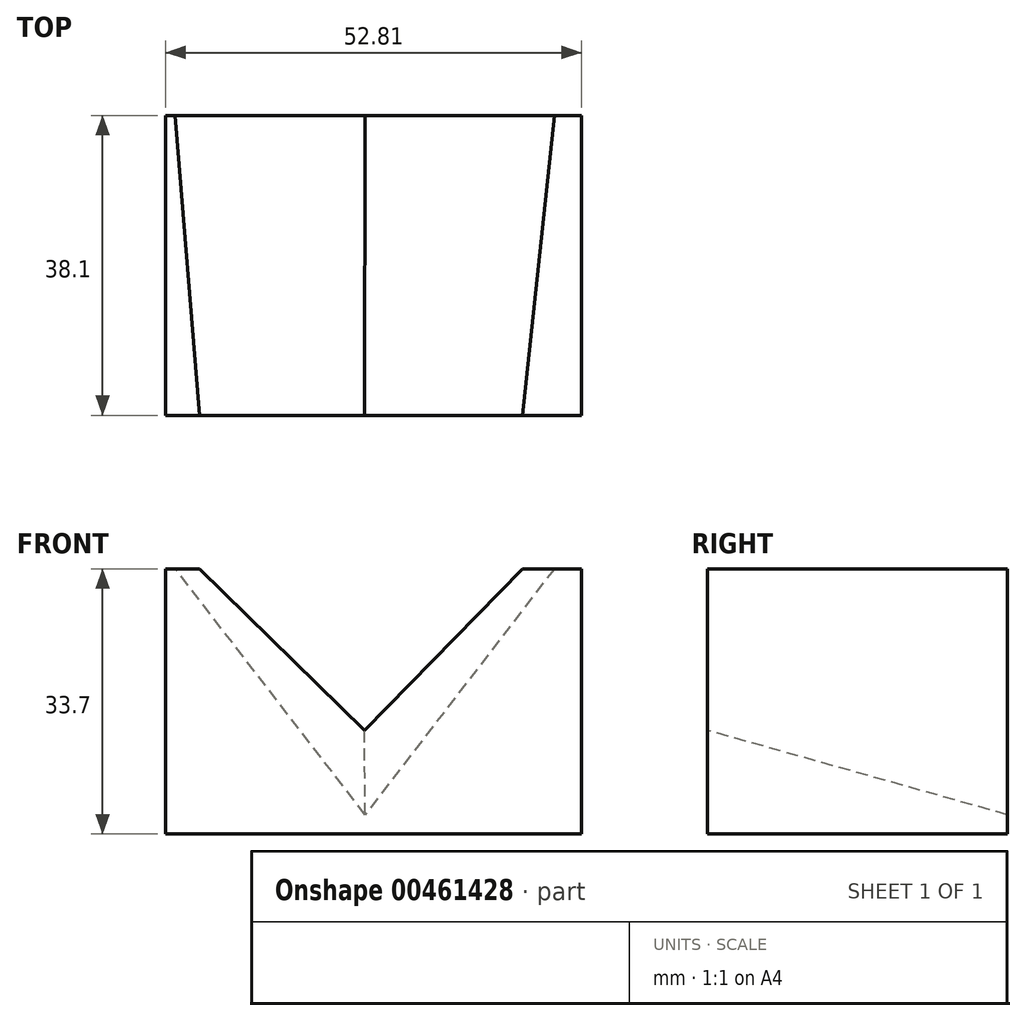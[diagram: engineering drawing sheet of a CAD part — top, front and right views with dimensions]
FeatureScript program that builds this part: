
annotation { "Feature Type Name" : "Feature", "Feature Type Description" : "" }
export const myFeature = defineFeature(function(context is Context, id is Id, definition is map)
    precondition{}
    {
        {
            var Q0;
            Q0=qCreatedBy(makeId("Front.planeOp"),FACE);
            var sketch = newSketch(context, id + "F0", { "sketchPlane" : qUnion([Q0])});
            skLineSegment(sketch, "E0.bottom", {"start": v(-31.33, 22.07) * mm, "end": v(21.48, 22.07) * mm});
            skLineSegment(sketch, "E0.top", {"start": v(-31.33, -11.63) * mm, "end": v(21.48, -11.63) * mm});
            skLineSegment(sketch, "E0.left", {"start": v(-31.33, 22.07) * mm, "end": v(-31.33, -11.63) * mm});
            skLineSegment(sketch, "E0.right", {"start": v(21.48, 22.07) * mm, "end": v(21.48, -11.63) * mm});
            skSolve(sketch);
        }
        {
            var Q0;
            Q0=makeQuery(id+"F0.imprint","IMPRINT",FACE,{"disambiguationData":[TD([[makeQuery(id+"F0.imprint","IMPRINT",EDGE,{"derivedFrom":sQuery(id+"F0.wireOp",EDGE,"E0.bottom")}),-1.0]])]});
            extrude(context, id + "F1", {"entities" : qUnion([Q0]), "depth" : 38.1 * mm});
        }
        {
            var Q0;
            Q0=makeQuery(id+"F1.opExtrude","CAP_FACE",FACE,{"disambiguationData":[OSD([sQuery(id+"F0.wireOp",EDGE,"E0.bottom"),sQuery(id+"F0.wireOp",EDGE,"E0.top"),sQuery(id+"F0.wireOp",EDGE,"E0.left"),sQuery(id+"F0.wireOp",EDGE,"E0.right")])],"isStart":false});
            var sketch = newSketch(context, id + "F2", { "sketchPlane" : qUnion([Q0])});
            skLineSegment(sketch, "E1", {"start": v(-27.05, 22.07) * mm, "end": v(-6.07, 1.54) * mm});
            skLineSegment(sketch, "E2", {"start": v(-6.07, 1.54) * mm, "end": v(14.02, 22.07) * mm});
            skSolve(sketch);
        }
        {
            var Q0;
            Q0=makeQuery(id+"F1.opExtrude","CAP_FACE",FACE,{"disambiguationData":[OSD([sQuery(id+"F0.wireOp",EDGE,"E0.bottom"),sQuery(id+"F0.wireOp",EDGE,"E0.top"),sQuery(id+"F0.wireOp",EDGE,"E0.left"),sQuery(id+"F0.wireOp",EDGE,"E0.right")])],"isStart":true});
            var sketch = newSketch(context, id + "F3", { "sketchPlane" : qUnion([Q0])});
            skLineSegment(sketch, "E3", {"start": v(-18.03, 22.07) * mm, "end": v(6, -9.16) * mm});
            skLineSegment(sketch, "E4", {"start": v(6, -9.16) * mm, "end": v(30.1, 22.07) * mm});
            skSolve(sketch);
        }
        {
            var Q1;
            {var subQ0=sQuery(id+"F3.wireOp",EDGE,"E3");Q1=makeQuery(id+"F3.imprint","IMPRINT",FACE,{"disambiguationData":[TD([[makeQuery(id+"F3.imprint","IMPRINT",EDGE,{"derivedFrom":subQ0}),1.0]])]});}
            var Q2;
            {var subQ0=sQuery(id+"F2.wireOp",EDGE,"E1");Q2=makeQuery(id+"F2.imprint","IMPRINT",FACE,{"disambiguationData":[TD([[makeQuery(id+"F2.imprint","IMPRINT",EDGE,{"derivedFrom":subQ0}),1.0]])]});}
            var Q3;
            {var subQ0=sQuery(id+"F3.wireOp",EDGE,"E3");Q3=makeQuery(id+"F3.imprint","IMPRINT",FACE,{"disambiguationData":[TD([[makeQuery(id+"F3.imprint","IMPRINT",EDGE,{"derivedFrom":subQ0}),1.0]])]});}
            var Q4;
            {var subQ0=sQuery(id+"F2.wireOp",EDGE,"E1");Q4=makeQuery(id+"F2.imprint","IMPRINT",FACE,{"disambiguationData":[TD([[makeQuery(id+"F2.imprint","IMPRINT",EDGE,{"derivedFrom":subQ0}),1.0]])]});}
            loft(context, id + "F4", {"operationType" : NewBodyOperationType.REMOVE, "sheetProfilesArray" : [{ "sheetProfileEntities" : qUnion([Q1]) }, { "sheetProfileEntities" : qUnion([Q2]) }], "wireProfilesArray" : [{ "wireProfileEntities" : qUnion([Q3]) }, { "wireProfileEntities" : qUnion([Q4]) }]});
        }
    });
